# Revit family: Medical_All_Hill-Rom_TruSystem-7000
name_source: partatom
category: Specialty Equipment
revit_build: Autodesk Revit Architecture 2015 (Build: 20140606_1530(x64)
units: mm (PartAtom-declared; Revit-internal decimal feet)

## types (1)
- TruSystem 7000 Surgical Table
    Adjustment Range Joint Back Section = +90°/– 45°
    Adjustment Range Joint Leg Section = +90°/–105°
    Ambient Temperature = +10°C to +40°C
    Apparent Load = 0 VA
    BIMobject category = All
    BIMobject category code = medical-all
    BIMobject main category = Medical
    BIMobject main category code = medical
    Batteries = IPS, 2 rechargeable batteries, 40.7 V/4.8Ah
    Brand url = https://construction.hill-rom.com
    Cap Material = Plastic-Hill-Rom-Light Blue
    Default Elevation = 4' - 0"
    Depth = 0' - 0"
    Description = TruSystem® 7000 Operating Table is made for various applications and surgical procedures in today's ORs allowing you and your team can concentrate on the patient - not on the surgical equipment.
    Design country = United States
    Edition number = 1
    Frequency = 50 Hz
    Frequency Range = 50-60 Hz
    Full Load Current = 20 A
    Height = 0' - 0"
    Height Adjustment Max. = 3' - 9"
    Height Adjustment Min. = 1' - 11"
    Installation instructions = https://construction.hill-rom.com
    Length = 3' - 10 1/16"
    Lift Material = Leather-Hill-Rom-Black
    Longitudinal Slide = 1' - 6"
    Manufacturer = Hill-Rom
    Manufacturer country = United States
    Manufacturer name = Hill-Rom
    Model = TruSystem® 7000 OR Table
    Nominal height = 0' - 0"
    Nominal width = 0' - 0"
    Patient Weight Capacity = 1000.00 lb
    Power Consumption (max) = 700 W
    Power Factor = 1
    Product Guid = 5b24c543-3ac1-4593-824c-c6b656ada701
    Product SKU = Trumpf-TruSystem7000
    Product data url = https://bimobject.com
    Product family = OR Tables
    Product group = TruSystem7000
    Product url = https://www.trumpfmedical.com
    QR code = http://bimobject.com
    Rail Material = Steel-Hill-Rom-Stainless
    Relative humidity = 20% to 80%
    Running Gear Material = Steel-Hill-Rom-Stainless
    Support Material = Steel-Hill-Rom-Stainless
    Table Top Material = Fabric-Hill-Rom-Black
    Table Top Overall = 79.3" x 23.6"
    Technical description = https://construction.hill-rom.com
    Tilting = 30.00°
    Trendelenburg / Reverse Trendelenburg = 45.00°
    URL = https://www.hill-rom.com
    Voltage = 240 V
    Voltage Range = 100-240 V
    Weight = 661.00 lb
    Weight Net (Kg) = 0
    Wheel Cap Material = Plastic-Hill-Rom-Grey Blue
    Wheel Material = Plastic-Hill-Rom-Gray
    Width = 1' - 11 5/8"
    Youtube clip = https://www.youtube.com
    Zero Position = Simultaneous leveling of all sections

## geometry (parser evidence)
native form markers: Blend x8, Sweep x2
no freeform markers — native parametric forms only
